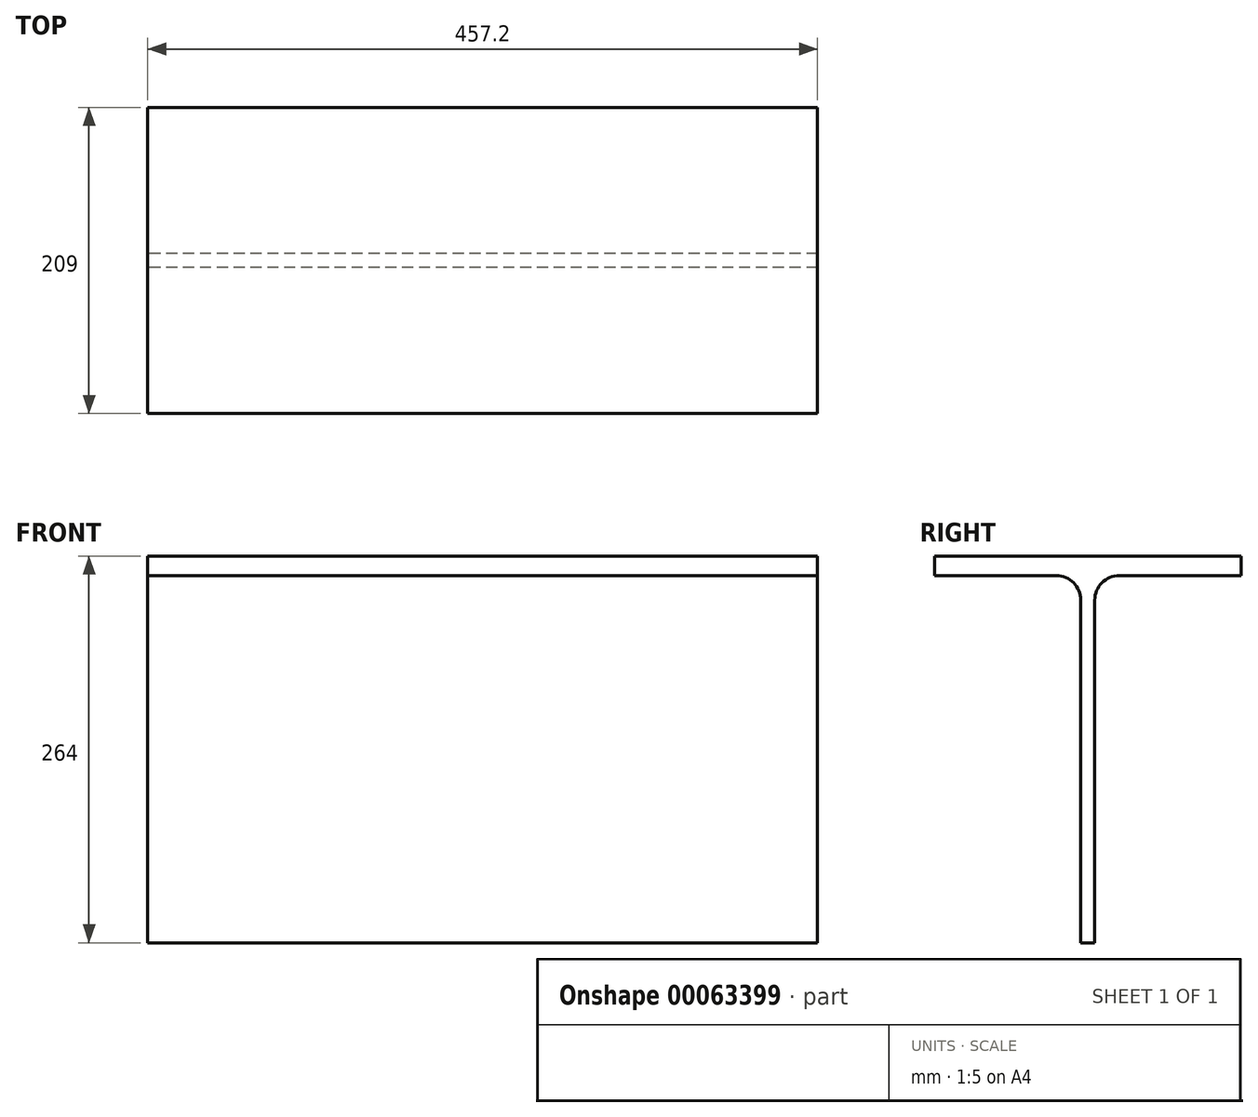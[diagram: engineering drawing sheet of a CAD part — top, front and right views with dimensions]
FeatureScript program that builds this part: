
annotation { "Feature Type Name" : "Feature", "Feature Type Description" : "" }
export const myFeature = defineFeature(function(context is Context, id is Id, definition is map)
    precondition{}
    {
        {
            var Q0;
            Q0=qCreatedBy(makeId("Right.planeOp"),FACE);
            var sketch = newSketch(context, id + "F0", { "sketchPlane" : qUnion([Q0])});
            skLineSegment(sketch, "E0", {"start": v(-4.75, 0) * mm, "end": v(-4.75, 233.99) * mm});
            skLineSegment(sketch, "E1", {"start": v(-21.46, 250.7) * mm, "end": v(-104.5, 250.7) * mm});
            skLineSegment(sketch, "E2", {"start": v(-104.5, 250.7) * mm, "end": v(-104.5, 264) * mm});
            skLineSegment(sketch, "E3", {"start": v(-104.5, 264) * mm, "end": v(0, 264) * mm});
            skPoint(sketch, "E4.visualSharp", {"position": v(-4.75, 250.7) * mm});
            skArc(sketch, "E4.filletArc", {"start": v(-4.75, 233.99) * mm, "mid": v(-9.64, 245.8) * mm, "end": v(-21.46, 250.7) * mm});
            skLineSegment(sketch, "E5.MirrorCS", {"start": v(4.75, 0) * mm, "end": v(4.75, 233.99) * mm});
            skLineSegment(sketch, "E6.MirrorCS", {"start": v(21.46, 250.7) * mm, "end": v(104.5, 250.7) * mm});
            skArc(sketch, "E7.MirrorCS", {"start": v(4.75, 233.99) * mm, "mid": v(9.64, 245.8) * mm, "end": v(21.46, 250.7) * mm});
            skLineSegment(sketch, "E8.MirrorCS", {"start": v(104.5, 264) * mm, "end": v(0, 264) * mm});
            skPoint(sketch, "E9.MirrorP", {"position": v(4.75, 250.7) * mm});
            skLineSegment(sketch, "E10.MirrorCS", {"start": v(104.5, 250.7) * mm, "end": v(104.5, 264) * mm});
            skLineSegment(sketch, "E11", {"start": v(-4.75, 0) * mm, "end": v(4.75, 0) * mm});
            skSolve(sketch);
        }
        {
            var Q0;
            Q0 = qSketchRegion(id + "F0", true);
            extrude(context, id + "F1", {"entities" : qUnion([Q0]), "depth" : 457.2 * mm});
        }
    });
